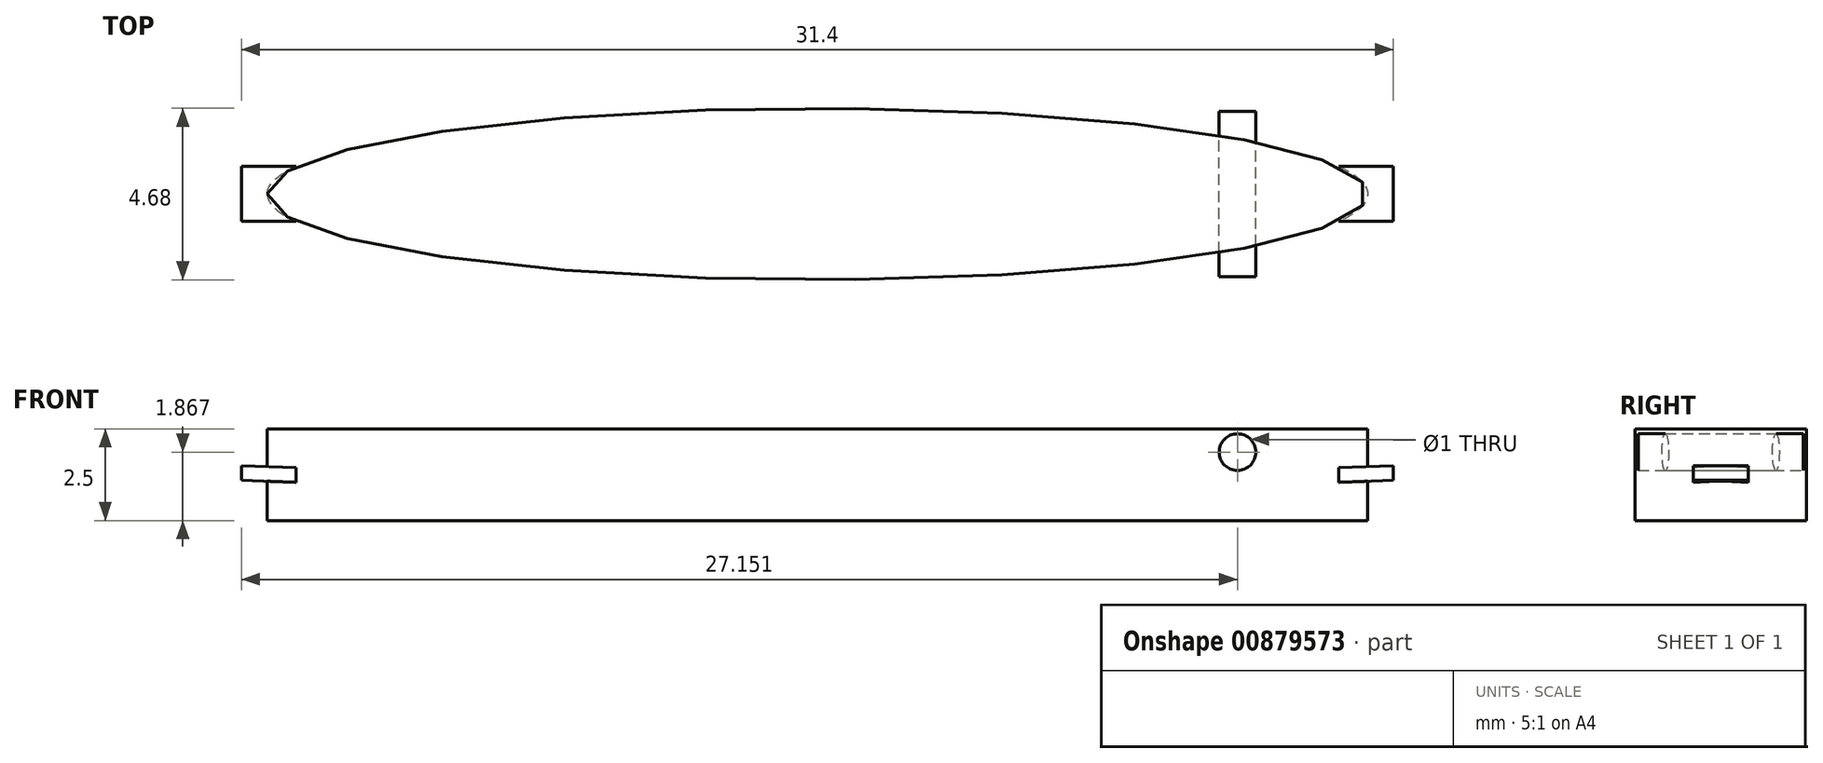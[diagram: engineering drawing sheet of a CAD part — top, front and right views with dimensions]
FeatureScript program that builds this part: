
annotation { "Feature Type Name" : "Feature", "Feature Type Description" : "" }
export const myFeature = defineFeature(function(context is Context, id is Id, definition is map)
    precondition{}
    {
        {
            var Q0;
            Q0=qCreatedBy(makeId("Top.planeOp"),FACE);
            var sketch = newSketch(context, id + "F0", { "sketchPlane" : qUnion([Q0])});
            skEllipse(sketch, "E0", {"center": v(0, 0) * mm, "majorRadius": 15 * mm, "minorRadius": 2.34 * mm, "majorAxis": v(-1, 0)});
            skPoint(sketch, "E1", {"position": v(-15, 0) * mm});
            skPoint(sketch, "E2", {"position": v(15, 0) * mm});
            skPoint(sketch, "E3", {"position": v(0, 2.34) * mm});
            skPoint(sketch, "E4", {"position": v(0, -2.34) * mm});
            skLineSegment(sketch, "E5", {"start": v(-15, 0) * mm, "end": v(15, 0) * mm, "construction": true});
            skLineSegment(sketch, "E6", {"start": v(-12.88, 0) * mm, "end": v(12.88, 0) * mm, "construction": true});
            skLineSegment(sketch, "E7", {"start": v(0, 0) * mm, "end": v(-12.88, 0) * mm, "construction": true});
            skLineSegment(sketch, "E8", {"start": v(-12.88, 0) * mm, "end": v(-12.88, -2.7) * mm, "construction": true});
            skLineSegment(sketch, "E9", {"start": v(-12.88, -2.7) * mm, "end": v(0, -2.7) * mm, "construction": true});
            skLineSegment(sketch, "E10", {"start": v(0, -2.7) * mm, "end": v(0, 0) * mm, "construction": true});
            skPoint(sketch, "E11", {"position": v(-12.88, -1.2) * mm});
            skLineSegment(sketch, "E12", {"start": v(-12.88, -1.2) * mm, "end": v(-12.88, 0) * mm, "construction": true});
            skLineSegment(sketch, "E13", {"start": v(-12.88, -1.2) * mm, "end": v(-12.53, -1.2) * mm, "construction": true});
            skLineSegment(sketch, "E14", {"start": v(-12.53, -1.2) * mm, "end": v(-12.53, 0) * mm, "construction": true});
            skFitSpline(sketch, "E15.0", {"points": [v(-15.95, 0.43) * mm, v(-16.02, 0) * mm, v(-15.95, -0.43) * mm, v(-15.78, -0.78) * mm, v(-15.56, -1.04) * mm, v(-15.25, -1.32) * mm, v(-14.83, -1.58) * mm, v(-14.23, -1.83) * mm, v(-13.53, -2.07) * mm, v(-12.71, -2.28) * mm, v(-11.8, -2.47) * mm, v(-10.44, -2.7) * mm, v(-8.89, -2.9) * mm, v(-7.16, -3.06) * mm, v(-5.36, -3.2) * mm, v(-3.46, -3.29) * mm, v(-1.5, -3.33) * mm, v(0, -3.34) * mm, v(1.5, -3.33) * mm, v(3.46, -3.29) * mm, v(5.36, -3.2) * mm, v(7.16, -3.06) * mm, v(8.89, -2.9) * mm, v(10.44, -2.7) * mm, v(11.8, -2.47) * mm, v(12.71, -2.28) * mm, v(13.53, -2.07) * mm, v(14.23, -1.83) * mm, v(14.83, -1.58) * mm, v(15.25, -1.32) * mm, v(15.56, -1.04) * mm, v(15.78, -0.78) * mm, v(15.95, -0.43) * mm, v(16.02, 0) * mm, v(15.95, 0.43) * mm, v(15.78, 0.78) * mm, v(15.56, 1.04) * mm, v(15.25, 1.32) * mm, v(14.83, 1.58) * mm, v(14.23, 1.83) * mm, v(13.53, 2.07) * mm, v(12.71, 2.28) * mm, v(11.8, 2.47) * mm, v(10.44, 2.7) * mm, v(8.89, 2.9) * mm, v(7.16, 3.06) * mm, v(5.36, 3.2) * mm, v(3.46, 3.29) * mm, v(1.5, 3.33) * mm, v(0, 3.34) * mm, v(-1.5, 3.33) * mm, v(-3.46, 3.29) * mm, v(-5.36, 3.2) * mm, v(-7.16, 3.06) * mm, v(-8.89, 2.9) * mm, v(-10.44, 2.7) * mm, v(-11.8, 2.47) * mm, v(-12.71, 2.28) * mm, v(-13.53, 2.07) * mm, v(-14.23, 1.83) * mm, v(-14.83, 1.58) * mm, v(-15.25, 1.32) * mm, v(-15.56, 1.04) * mm, v(-15.78, 0.78) * mm, v(-15.95, 0.43) * mm, v(-16.02, 0) * mm, v(-15.95, -0.43) * mm, v(-15.95, 0.43) * mm]});
            skPoint(sketch, "E16", {"position": v(0, -3.34) * mm});
            skPoint(sketch, "E17", {"position": v(0, 3.34) * mm});
            skPoint(sketch, "E18", {"position": v(-16, 0) * mm});
            skPoint(sketch, "E19", {"position": v(16, 0) * mm});
            skSolve(sketch);
        }
        {
            var Q0;
            Q0 = qSketchRegion(id + "F0", true);
            extrude(context, id + "F1", {"entities" : qUnion([Q0]), "oppositeDirection" : true, "depth" : 1.5 * mm, "offsetDistance" : 25 * mm});
        }
        {
            var Q0;
            Q0=qCreatedBy(makeId("Front.planeOp"),FACE);
            var sketch = newSketch(context, id + "F2", { "sketchPlane" : qUnion([Q0])});
            skLineSegment(sketch, "E20", {"start": v(15.7, 0) * mm, "end": v(0.8, -0.57) * mm});
            skLineSegment(sketch, "E21", {"start": v(0.8, -0.57) * mm, "end": v(0.82, -0.97) * mm});
            skLineSegment(sketch, "E22", {"start": v(0.82, -0.97) * mm, "end": v(15.7, -0.4) * mm});
            skLineSegment(sketch, "E23", {"start": v(15.7, -0.4) * mm, "end": v(15.7, 0) * mm});
            skLineSegment(sketch, "E24", {"start": v(15.7, 0) * mm, "end": v(0.8, 0) * mm, "construction": true});
            skLineSegment(sketch, "E25", {"start": v(0.8, 0) * mm, "end": v(0, 0) * mm, "construction": true});
            skLineSegment(sketch, "E26", {"start": v(0, 0) * mm, "end": v(0, -2.93) * mm, "construction": true});
            skLineSegment(sketch, "E27.MirrorCS", {"start": v(-0.8, -0.57) * mm, "end": v(-0.82, -0.97) * mm});
            skLineSegment(sketch, "E28.MirrorCS", {"start": v(-0.82, -0.97) * mm, "end": v(-15.7, -0.4) * mm});
            skLineSegment(sketch, "E29.MirrorCS", {"start": v(-15.7, 0) * mm, "end": v(-0.8, -0.57) * mm});
            skLineSegment(sketch, "E30.MirrorCS", {"start": v(-15.7, -0.4) * mm, "end": v(-15.7, 0) * mm});
            skLineSegment(sketch, "E31", {"start": v(0.8, 0) * mm, "end": v(0.8, -0.57) * mm, "construction": true});
            skSolve(sketch);
        }
        {
            var Q0;
            Q0=makeQuery(id+"F2.imprint","IMPRINT",FACE,{"disambiguationData":[TD([[makeQuery(id+"F2.imprint","IMPRINT",EDGE,{"derivedFrom":sQuery(id+"F2.wireOp",EDGE,"E20")}),1.0]])]});
            var Q1;
            Q1=makeQuery(id+"F2.imprint","IMPRINT",FACE,{"disambiguationData":[TD([[makeQuery(id+"F2.imprint","IMPRINT",EDGE,{"derivedFrom":sQuery(id+"F2.wireOp",EDGE,"E27.MirrorCS")}),-1.0]])]});
            extrude(context, id + "F3", {"entities" : qUnion([Q0, Q1]), "operationType" : NewBodyOperationType.ADD, "endBound" : BoundingType.SYMMETRIC, "oppositeDirection" : true, "depth" : 1.5 * mm, "offsetDistance" : 25 * mm});
        }
        {
            var Q0;
            Q0=makeQuery(id+"F1.opExtrude","CAP_FACE",FACE,{"disambiguationData":[OSD([sQuery(id+"F0.wireOp",EDGE,"E0"),sQuery(id+"F0.wireOp",EDGE,"E15.0")])],"isStart":true});
            var sketch = newSketch(context, id + "F4", { "sketchPlane" : qUnion([Q0])});
            skEllipse(sketch, "E32", {"center": v(0, 0) * mm, "majorRadius": 15 * mm, "minorRadius": 2.34 * mm, "majorAxis": v(-1, 0)});
            skPoint(sketch, "E33", {"position": v(-15, 0) * mm});
            skPoint(sketch, "E34", {"position": v(15, 0) * mm});
            skPoint(sketch, "E35", {"position": v(0, 2.34) * mm});
            skPoint(sketch, "E36", {"position": v(0, -2.34) * mm});
            skLineSegment(sketch, "E37", {"start": v(-15, 0) * mm, "end": v(15, 0) * mm, "construction": true});
            skLineSegment(sketch, "E38", {"start": v(-12.88, 0) * mm, "end": v(12.88, 0) * mm, "construction": true});
            skLineSegment(sketch, "E39", {"start": v(0, 0) * mm, "end": v(-12.88, 0) * mm, "construction": true});
            skLineSegment(sketch, "E40", {"start": v(-12.88, 0) * mm, "end": v(-12.88, -2.7) * mm, "construction": true});
            skLineSegment(sketch, "E41", {"start": v(-12.88, -2.7) * mm, "end": v(0, -2.7) * mm, "construction": true});
            skLineSegment(sketch, "E42", {"start": v(0, -2.7) * mm, "end": v(0, 0) * mm, "construction": true});
            skPoint(sketch, "E43", {"position": v(-12.88, -1.2) * mm});
            skLineSegment(sketch, "E44", {"start": v(-12.88, -1.2) * mm, "end": v(-12.88, 0) * mm, "construction": true});
            skLineSegment(sketch, "E45", {"start": v(-12.88, -1.2) * mm, "end": v(-12.53, -1.2) * mm, "construction": true});
            skLineSegment(sketch, "E46", {"start": v(-12.53, -1.2) * mm, "end": v(-12.53, 0) * mm, "construction": true});
            skFitSpline(sketch, "E47.0", {"points": [v(-15.95, 0.43) * mm, v(-16.02, 0) * mm, v(-15.95, -0.43) * mm, v(-15.78, -0.78) * mm, v(-15.56, -1.04) * mm, v(-15.25, -1.32) * mm, v(-14.83, -1.58) * mm, v(-14.23, -1.83) * mm, v(-13.53, -2.07) * mm, v(-12.71, -2.28) * mm, v(-11.8, -2.47) * mm, v(-10.44, -2.7) * mm, v(-8.89, -2.9) * mm, v(-7.16, -3.06) * mm, v(-5.36, -3.2) * mm, v(-3.46, -3.29) * mm, v(-1.5, -3.33) * mm, v(0, -3.34) * mm, v(1.5, -3.33) * mm, v(3.46, -3.29) * mm, v(5.36, -3.2) * mm, v(7.16, -3.06) * mm, v(8.89, -2.9) * mm, v(10.44, -2.7) * mm, v(11.8, -2.47) * mm, v(12.71, -2.28) * mm, v(13.53, -2.07) * mm, v(14.23, -1.83) * mm, v(14.83, -1.58) * mm, v(15.25, -1.32) * mm, v(15.56, -1.04) * mm, v(15.78, -0.78) * mm, v(15.95, -0.43) * mm, v(16.02, 0) * mm, v(15.95, 0.43) * mm, v(15.78, 0.78) * mm, v(15.56, 1.04) * mm, v(15.25, 1.32) * mm, v(14.83, 1.58) * mm, v(14.23, 1.83) * mm, v(13.53, 2.07) * mm, v(12.71, 2.28) * mm, v(11.8, 2.47) * mm, v(10.44, 2.7) * mm, v(8.89, 2.9) * mm, v(7.16, 3.06) * mm, v(5.36, 3.2) * mm, v(3.46, 3.29) * mm, v(1.5, 3.33) * mm, v(0, 3.34) * mm, v(-1.5, 3.33) * mm, v(-3.46, 3.29) * mm, v(-5.36, 3.2) * mm, v(-7.16, 3.06) * mm, v(-8.89, 2.9) * mm, v(-10.44, 2.7) * mm, v(-11.8, 2.47) * mm, v(-12.71, 2.28) * mm, v(-13.53, 2.07) * mm, v(-14.23, 1.83) * mm, v(-14.83, 1.58) * mm, v(-15.25, 1.32) * mm, v(-15.56, 1.04) * mm, v(-15.78, 0.78) * mm, v(-15.95, 0.43) * mm, v(-16.02, 0) * mm, v(-15.95, -0.43) * mm, v(-15.95, 0.43) * mm]});
            skSolve(sketch);
        }
        {
            var Q0;
            Q0 = qSketchRegion(id + "F4", true);
            extrude(context, id + "F5", {"entities" : qUnion([Q0]), "operationType" : NewBodyOperationType.ADD, "depth" : 1 * mm, "offsetDistance" : 25 * mm});
        }
        {
            var Q0;
            Q0=qCreatedBy(makeId("Front.planeOp"),FACE);
            var sketch = newSketch(context, id + "F6", { "sketchPlane" : qUnion([Q0])});
            skLineSegment(sketch, "E48", {"start": v(0, 0) * mm, "end": v(11.5, 0) * mm, "construction": true});
            skLineSegment(sketch, "E49", {"start": v(11.5, 0) * mm, "end": v(11.52, -0.13) * mm, "construction": true});
            skLineSegment(sketch, "E50", {"start": v(11.52, -0.13) * mm, "end": v(11.45, 0.37) * mm, "construction": true});
            skCircle(sketch, "E51", {"center": v(11.45, 0.37) * mm, "radius": 0.5 * mm});
            skLineSegment(sketch, "E52", {"start": v(0, 0) * mm, "end": v(0, 1.38) * mm, "construction": true});
            skCircle(sketch, "E53.MirrorC", {"center": v(-11.45, 0.37) * mm, "radius": 0.5 * mm});
            skSolve(sketch);
        }
        {
            var Q0;
            Q0=makeQuery(id+"F6.imprint","IMPRINT",FACE,{"disambiguationData":[TD([[makeQuery(id+"F6.imprint","IMPRINT",EDGE,{"derivedFrom":sQuery(id+"F6.wireOp",EDGE,"E51")}),1.0]])]});
            var Q1;
            Q1=makeQuery(id+"F6.imprint","IMPRINT",FACE,{"disambiguationData":[TD([[makeQuery(id+"F6.imprint","IMPRINT",EDGE,{"derivedFrom":sQuery(id+"F6.wireOp",EDGE,"E53.MirrorC")}),-1.0]])]});
            extrude(context, id + "F7", {"entities" : qUnion([Q0, Q1]), "operationType" : NewBodyOperationType.REMOVE, "endBound" : BoundingType.SYMMETRIC, "depth" : 4.5 * mm, "offsetDistance" : 25 * mm});
        }
        {
            var Q0;
            Q0=makeQuery(id+"F6.imprint","IMPRINT",FACE,{"disambiguationData":[TD([[makeQuery(id+"F6.imprint","IMPRINT",EDGE,{"derivedFrom":sQuery(id+"F6.wireOp",EDGE,"E51")}),1.0]])]});
            var Q1;
            Q1=makeQuery(id+"F6.imprint","IMPRINT",FACE,{"disambiguationData":[TD([[makeQuery(id+"F6.imprint","IMPRINT",EDGE,{"derivedFrom":sQuery(id+"F6.wireOp",EDGE,"E53.MirrorC")}),-1.0]])]});
            extrude(context, id + "F8", {"entities" : qUnion([Q0, Q1]), "endBound" : BoundingType.SYMMETRIC, "depth" : 4.5 * mm, "offsetDistance" : 25 * mm});
        }
    });
